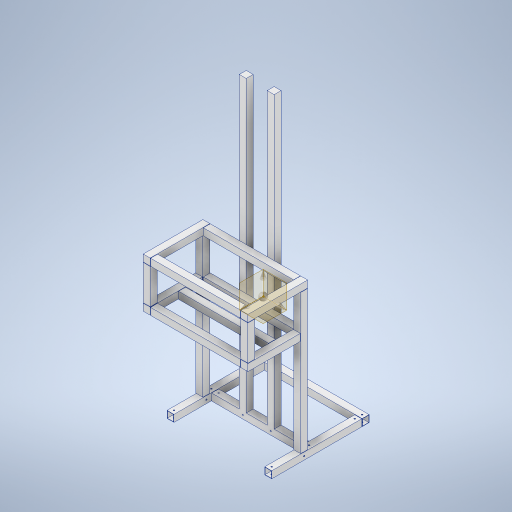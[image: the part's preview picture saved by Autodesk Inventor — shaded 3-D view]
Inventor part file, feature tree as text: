
AUTODESK INVENTOR PART (.ipt)
format: ipt  version: 2023 (Build 270158000, 158)  size: 645,632 bytes
history: native  units: mm
features: extrude x17, other x12, sketch x11
ambient origin geometry x8: Origin, YZ Plane, XZ Plane, XY Plane, X Axis, Y Axis, Z Axis, Center Point
bodies: Body1 (feature_tree)
feature tree (40):
  other  "Твердое тело1"
  other  "РабПлоскость2"
  other  "РабПлоскость6"
  extrude  "Выдавливание10"  Depth=600.0mm
  extrude  "Выдавливание20"  Depth=300.0mm
  other  "РабПлоскость16"
  extrude  "Выдавливание21"  Depth=40.0mm
  extrude  "Выдавливание25"  Depth=2.0mm
  other  "РабПлоскость12"
  extrude  "Выдавливание26"  Depth=40.0mm
  other  "РабПлоскость22"
  other  "РабПлоскость15"
  extrude  "Выдавливание28"  Depth=40.0mm
  other  "РабПлоскость18"
  other  "РабПлоскость21"
  extrude  "Выдавливание36"  Depth=300.0mm
  extrude  "Выдавливание37"  Depth=2.0mm
  other  "РабПлоскость23"
  extrude  "Выдавливание38"  Depth=216.0mm
  other  "РабПлоскость24"
  extrude  "Выдавливание39"  Depth=40.0mm TaperAngle=0.0deg
  other  "РабПлоскость25"
  extrude  "Выдавливание40"  Depth=100.0mm
  extrude  "Выдавливание41"  Depth=2.0mm
  extrude  "Выдавливание42"  Depth=200.0mm
  extrude  "Выдавливание43"  Depth=40.0mm
  extrude  "Выдавливание44"  Depth=40.0mm
  extrude  "Выдавливание45"  Depth=40.0mm
  extrude  "Выдавливание46"  Depth=40.0mm
  sketch  "Эскиз30"
  sketch  "Эскиз41"
  sketch  "Эскиз42"
  sketch  "Эскиз43"
  sketch  "Эскиз44"
  sketch  "Эскиз45"
  sketch  "Эскиз46"
  sketch  "Эскиз47"
  sketch  "Эскиз48"
  sketch  "Эскиз49"
  sketch  "Эскиз50"
